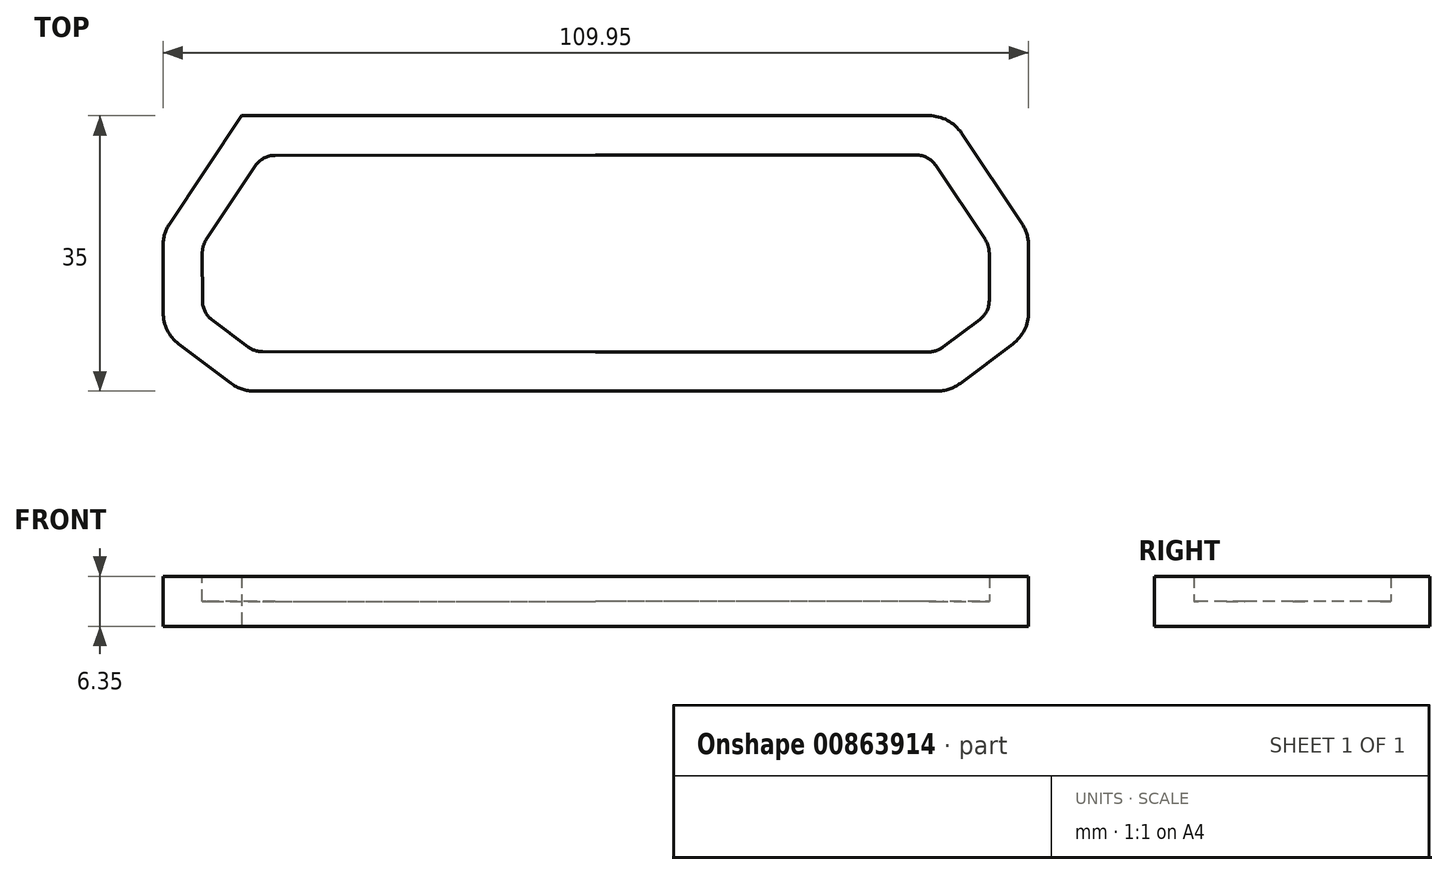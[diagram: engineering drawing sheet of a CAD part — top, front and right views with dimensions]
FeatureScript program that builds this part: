
annotation { "Feature Type Name" : "Feature", "Feature Type Description" : "" }
export const myFeature = defineFeature(function(context is Context, id is Id, definition is map)
    precondition{}
    {
        {
            var Q0;
            Q0=qCreatedBy(makeId("Top.planeOp"),FACE);
            var sketch = newSketch(context, id + "F0", { "sketchPlane" : qUnion([Q0])});
            skLineSegment(sketch, "E0", {"start": v(45, 17.5) * mm, "end": v(54.98, 2.52) * mm});
            skLineSegment(sketch, "E1", {"start": v(54.98, 2.52) * mm, "end": v(54.98, -9.98) * mm});
            skLineSegment(sketch, "E2", {"start": v(54.98, -9.98) * mm, "end": v(45, -17.5) * mm});
            skLineSegment(sketch, "E3", {"start": v(45, -17.5) * mm, "end": v(0, -17.5) * mm});
            skLineSegment(sketch, "E4", {"start": v(45, 17.5) * mm, "end": v(0, 17.5) * mm});
            skLineSegment(sketch, "E5", {"start": v(0, 17.5) * mm, "end": v(0, -17.5) * mm});
            skLineSegment(sketch, "E6.MirrorCS", {"start": v(-45.04, 17.46) * mm, "end": v(-0.04, 17.5) * mm});
            skLineSegment(sketch, "E7.MirrorCS", {"start": v(-45, 17.5) * mm, "end": v(-54.98, 2.52) * mm});
            skLineSegment(sketch, "E8.MirrorCS", {"start": v(-54.97, 2.5) * mm, "end": v(-54.95, -10) * mm});
            skLineSegment(sketch, "E9.MirrorCS", {"start": v(-54.98, -9.98) * mm, "end": v(-45, -17.5) * mm});
            skLineSegment(sketch, "E10.MirrorCS", {"start": v(-45.03, -17.48) * mm, "end": v(-0.03, -17.5) * mm});
            skLineSegment(sketch, "E11.0", {"start": v(-42.35, 12.46) * mm, "end": v(0, 12.5) * mm});
            skLineSegment(sketch, "E11.1", {"start": v(42.32, 12.5) * mm, "end": v(0, 12.5) * mm});
            skLineSegment(sketch, "E11.2", {"start": v(-42.35, 12.46) * mm, "end": v(-49.97, 1.03) * mm});
            skLineSegment(sketch, "E11.3", {"start": v(42.32, 12.5) * mm, "end": v(49.98, 1) * mm});
            skLineSegment(sketch, "E11.4", {"start": v(49.98, 1) * mm, "end": v(49.98, -7.48) * mm});
            skLineSegment(sketch, "E11.5", {"start": v(49.98, -7.48) * mm, "end": v(43.33, -12.5) * mm});
            skLineSegment(sketch, "E11.6", {"start": v(-49.97, 1.03) * mm, "end": v(-49.95, -7.5) * mm});
            skLineSegment(sketch, "E11.7", {"start": v(-49.95, -7.5) * mm, "end": v(-43.35, -12.48) * mm});
            skLineSegment(sketch, "E11.8", {"start": v(-43.35, -12.48) * mm, "end": v(0, -12.5) * mm});
            skLineSegment(sketch, "E11.9", {"start": v(43.33, -12.5) * mm, "end": v(0, -12.5) * mm});
            skLineSegment(sketch, "E12", {"start": v(0, 17.5) * mm, "end": v(-45, 17.5) * mm});
            skLineSegment(sketch, "E13", {"start": v(-45, 17.5) * mm, "end": v(-54.97, 2.5) * mm});
            skLineSegment(sketch, "E14", {"start": v(-54.95, -10) * mm, "end": v(-45, -17.5) * mm});
            skLineSegment(sketch, "E15", {"start": v(-45, -17.5) * mm, "end": v(0, -17.5) * mm});
            skSolve(sketch);
        }
        {
            var Q0;
            Q0=makeQuery(id+"F0.imprint","IMPRINT",FACE,{"disambiguationData":[TD([[makeQuery(id+"F0.imprint","IMPRINT",EDGE,{"derivedFrom":sQuery(id+"F0.wireOp",EDGE,"E5")}),-1.0]])]});
            var Q1;
            Q1=makeQuery(id+"F0.imprint","IMPRINT",FACE,{"disambiguationData":[TD([[makeQuery(id+"F0.imprint","IMPRINT",EDGE,{"derivedFrom":sQuery(id+"F0.wireOp",EDGE,"E0")}),-1.0]])]});
            var Q2;
            {var subQ6=sQuery(id+"F0.wireOp",EDGE,"E2");Q2=makeQuery(id+"F0.imprint","IMPRINT",FACE,{"disambiguationData":[TD([[makeQuery(id+"F0.imprint","IMPRINT",EDGE,{"derivedFrom":subQ6}),-1.0]])]});}
            extrude(context, id + "F1", {"entities" : qUnion([Q0, Q1, Q2]), "depth" : 6.35 * mm, "offsetDistance" : 25.4 * mm});
        }
        {
            var Q0;
            {var subQ5=sQuery(id+"F0.wireOp",EDGE,"VzqP0NJX-yZrj-hRN3-vbBe-lvKmNAORx1Dw");Q0=makeQuery(id+"F0.imprint","IMPRINT",FACE,{"disambiguationData":[TD([[makeQuery(id+"F0.imprint","IMPRINT",EDGE,{"derivedFrom":subQ5}),1.0]])]});}
            var Q1;
            {var subQ3=sQuery(id+"F0.wireOp",EDGE,"E5");var subQ6=sQuery(id+"F0.wireOp",EDGE,"SvXsJxY8-g8Aa-q47Y-NpeJ-hUn25gKxKZdq");var subQ8=makeQuery(id+"F0.imprint","INTERSECT",VERTEX,{"derivedFrom":[subQ3,subQ6]});Q1=makeQuery(id+"F0.imprint","IMPRINT",FACE,{"disambiguationData":[TD([[makeQuery(id+"F0.imprint","IMPRINT",EDGE,{"disambiguationData":[TD([[subQ8,-1.0]])],"derivedFrom":subQ3}),1.0]])]});}
            var Q2;
            {var subQ0=sQuery(id+"F0.wireOp",EDGE,"hUwyKqop-Jph7-GYIu-v7CJ-J6fjRY4b1OuN");Q2=makeQuery(id+"F0.imprint","IMPRINT",FACE,{"disambiguationData":[TD([[makeQuery(id+"F0.imprint","IMPRINT",EDGE,{"derivedFrom":subQ0}),1.0]])]});}
            var Q3;
            {var subQ0=sQuery(id+"F0.wireOp",EDGE,"E11.0");Q3=makeQuery(id+"F0.imprint","IMPRINT",FACE,{"disambiguationData":[TD([[makeQuery(id+"F0.imprint","IMPRINT",EDGE,{"derivedFrom":subQ0}),-1.0]])]});}
            var Q4;
            {var subQ0=sQuery(id+"F0.wireOp",EDGE,"E11.1");Q4=makeQuery(id+"F0.imprint","IMPRINT",FACE,{"disambiguationData":[TD([[makeQuery(id+"F0.imprint","IMPRINT",EDGE,{"derivedFrom":subQ0}),1.0]])]});}
            extrude(context, id + "F2", {"entities" : qUnion([Q0, Q1, Q2, Q3, Q4]), "operationType" : NewBodyOperationType.ADD, "depth" : 3.17 * mm, "offsetDistance" : 25.4 * mm});
        }
        {
            var Q0;
            Q0=makeQuery(id+"F1.opExtrude","SWEPT_EDGE",EDGE,{"disambiguationData":[OSD([sQuery(id+"F0.wireOp",EDGE,"E10.MirrorCS"),sQuery(id+"F0.wireOp",EDGE,"E14")])]});
            var Q1;
            Q1=makeQuery(id+"F1.opExtrude","SWEPT_EDGE",EDGE,{"disambiguationData":[OSD([sQuery(id+"F0.wireOp",EDGE,"E6.MirrorCS"),sQuery(id+"F0.wireOp",EDGE,"E13")])]});
            var Q2;
            Q2=makeQuery(id+"F1.opExtrude","SWEPT_EDGE",EDGE,{"disambiguationData":[OSD([sQuery(id+"F0.wireOp",EDGE,"E0"),sQuery(id+"F0.wireOp",EDGE,"E4")])]});
            var Q3;
            Q3=makeQuery(id+"F1.opExtrude","SWEPT_EDGE",EDGE,{"disambiguationData":[OSD([sQuery(id+"F0.wireOp",EDGE,"E0"),sQuery(id+"F0.wireOp",EDGE,"E1")])]});
            var Q4;
            Q4=makeQuery(id+"F1.opExtrude","SWEPT_EDGE",EDGE,{"disambiguationData":[OSD([sQuery(id+"F0.wireOp",EDGE,"E1"),sQuery(id+"F0.wireOp",EDGE,"E2")])]});
            var Q5;
            Q5=makeQuery(id+"F1.opExtrude","SWEPT_EDGE",EDGE,{"disambiguationData":[OSD([sQuery(id+"F0.wireOp",EDGE,"E2"),sQuery(id+"F0.wireOp",EDGE,"E3")])]});
            var Q6;
            Q6=makeQuery(id+"F1.opExtrude","SWEPT_EDGE",EDGE,{"disambiguationData":[OSD([sQuery(id+"F0.wireOp",EDGE,"E13"),sQuery(id+"F0.wireOp",EDGE,"E8.MirrorCS")])]});
            var Q7;
            Q7=makeQuery(id+"F1.opExtrude","SWEPT_EDGE",EDGE,{"disambiguationData":[OSD([sQuery(id+"F0.wireOp",EDGE,"E8.MirrorCS"),sQuery(id+"F0.wireOp",EDGE,"E14")])]});
            fillet(context, id + "F3", {"entities" : qUnion([Q0, Q1, Q2, Q3, Q4, Q5, Q6, Q7]), "radius" : 5 * mm, "tangentPropagation" : true, "allowEdgeOverflow" : false});
        }
        {
            var Q0;
            Q0=makeQuery(id+"F1.opExtrude","SWEPT_EDGE",EDGE,{"disambiguationData":[OSD([sQuery(id+"F0.wireOp",EDGE,"E11.0"),sQuery(id+"F0.wireOp",EDGE,"E11.2")])]});
            var Q1;
            Q1=makeQuery(id+"F1.opExtrude","SWEPT_EDGE",EDGE,{"disambiguationData":[OSD([sQuery(id+"F0.wireOp",EDGE,"E11.2"),sQuery(id+"F0.wireOp",EDGE,"E11.6")])]});
            var Q2;
            Q2=makeQuery(id+"F1.opExtrude","SWEPT_EDGE",EDGE,{"disambiguationData":[OSD([sQuery(id+"F0.wireOp",EDGE,"E11.6"),sQuery(id+"F0.wireOp",EDGE,"E11.7")])]});
            var Q3;
            Q3=makeQuery(id+"F1.opExtrude","SWEPT_EDGE",EDGE,{"disambiguationData":[OSD([sQuery(id+"F0.wireOp",EDGE,"E11.7"),sQuery(id+"F0.wireOp",EDGE,"E11.8")])]});
            var Q4;
            Q4=makeQuery(id+"F1.opExtrude","SWEPT_EDGE",EDGE,{"disambiguationData":[OSD([sQuery(id+"F0.wireOp",EDGE,"E11.5"),sQuery(id+"F0.wireOp",EDGE,"E11.9")])]});
            var Q5;
            Q5=makeQuery(id+"F1.opExtrude","SWEPT_EDGE",EDGE,{"disambiguationData":[OSD([sQuery(id+"F0.wireOp",EDGE,"E11.4"),sQuery(id+"F0.wireOp",EDGE,"E11.5")])]});
            var Q6;
            Q6=makeQuery(id+"F1.opExtrude","SWEPT_EDGE",EDGE,{"disambiguationData":[OSD([sQuery(id+"F0.wireOp",EDGE,"E11.3"),sQuery(id+"F0.wireOp",EDGE,"E11.4")])]});
            var Q7;
            Q7=makeQuery(id+"F1.opExtrude","SWEPT_EDGE",EDGE,{"disambiguationData":[OSD([sQuery(id+"F0.wireOp",EDGE,"E11.1"),sQuery(id+"F0.wireOp",EDGE,"E11.3")])]});
            fillet(context, id + "F4", {"entities" : qUnion([Q0, Q1, Q2, Q3, Q4, Q5, Q6, Q7]), "radius" : 3 * mm, "tangentPropagation" : true, "allowEdgeOverflow" : false});
        }
    });
